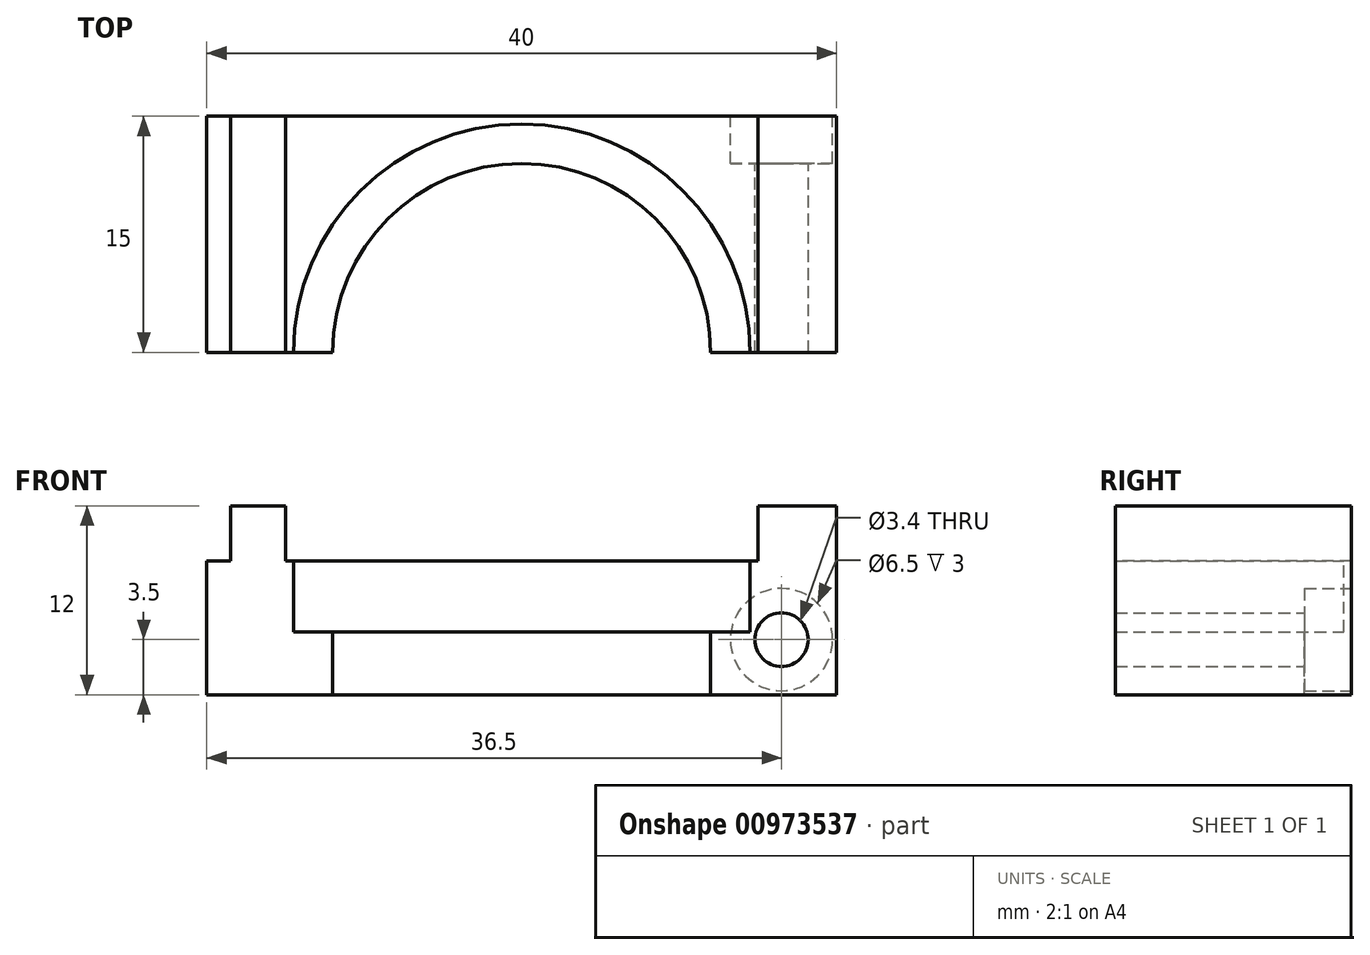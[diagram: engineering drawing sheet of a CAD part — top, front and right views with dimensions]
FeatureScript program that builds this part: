
annotation { "Feature Type Name" : "Feature", "Feature Type Description" : "" }
export const myFeature = defineFeature(function(context is Context, id is Id, definition is map)
    precondition{}
    {
        {
            var Q0;
            Q0=qCreatedBy(makeId("Top.planeOp"),FACE);
            var sketch = newSketch(context, id + "F0", { "sketchPlane" : qUnion([Q0])});
            skLineSegment(sketch, "E0.bottom", {"start": v(-20, 0) * mm, "end": v(20, 0) * mm});
            skLineSegment(sketch, "E0.top", {"start": v(-20, -15) * mm, "end": v(20, -15) * mm});
            skLineSegment(sketch, "E0.left", {"start": v(-20, 0) * mm, "end": v(-20, -15) * mm});
            skLineSegment(sketch, "E0.right", {"start": v(20, 0) * mm, "end": v(20, -15) * mm});
            skSolve(sketch);
        }
        {
            var Q0;
            Q0=makeQuery(id+"F0.imprint","IMPRINT",FACE,{"disambiguationData":[TD([[makeQuery(id+"F0.imprint","IMPRINT",EDGE,{"derivedFrom":sQuery(id+"F0.wireOp",EDGE,"E0.bottom")}),-1.0]])]});
            extrude(context, id + "F1", {"entities" : qUnion([Q0]), "depth" : 12 * mm, "offsetDistance" : 25 * mm});
        }
        {
            var Q0;
            Q0=makeQuery(id+"F1.opExtrude","CAP_FACE",FACE,{"disambiguationData":[OSD([sQuery(id+"F0.wireOp",EDGE,"E0.bottom"),sQuery(id+"F0.wireOp",EDGE,"E0.top"),sQuery(id+"F0.wireOp",EDGE,"E0.left"),sQuery(id+"F0.wireOp",EDGE,"E0.right")])],"isStart":false});
            var sketch = newSketch(context, id + "F2", { "sketchPlane" : qUnion([Q0])});
            skArc(sketch, "E1", {"start": v(14.5, -15) * mm, "mid": v(0, -0.5) * mm, "end": v(-14.5, -15) * mm});
            skSolve(sketch);
        }
        {
            var Q0;
            {var subQ0=sQuery(id+"F2.wireOp",EDGE,"E1");Q0=makeQuery(id+"F2.imprint","IMPRINT",FACE,{"disambiguationData":[TD([[makeQuery(id+"F2.imprint","IMPRINT",EDGE,{"derivedFrom":subQ0}),1.0]])]});}
            extrude(context, id + "F3", {"entities" : qUnion([Q0]), "operationType" : NewBodyOperationType.REMOVE, "oppositeDirection" : true, "depth" : 8 * mm, "offsetDistance" : 25 * mm});
        }
        {
            var Q0;
            Q0=makeQuery(id+"F3.boolean.opBoolean","COPY",FACE,{"derivedFrom":makeQuery(id+"F3.opExtrude","CAP_FACE",FACE,{"disambiguationData":[OSD([sQuery(id+"F0.wireOp",EDGE,"E0.top"),sQuery(id+"F2.wireOp",EDGE,"E1")])],"isStart":false})});
            var sketch = newSketch(context, id + "F4", { "sketchPlane" : qUnion([Q0])});
            skArc(sketch, "E2", {"start": v(12, -15) * mm, "mid": v(0, -3) * mm, "end": v(-12, -15) * mm});
            skSolve(sketch);
        }
        {
            var Q0;
            {var subQ0=sQuery(id+"F4.wireOp",EDGE,"E2");Q0=makeQuery(id+"F4.imprint","IMPRINT",FACE,{"disambiguationData":[TD([[makeQuery(id+"F4.imprint","IMPRINT",EDGE,{"derivedFrom":subQ0}),1.0]])]});}
            extrude(context, id + "F5", {"entities" : qUnion([Q0]), "operationType" : NewBodyOperationType.REMOVE, "endBound" : BoundingType.UP_TO_NEXT, "oppositeDirection" : true, "depth" : 25 * mm, "offsetDistance" : 25 * mm});
        }
        {
            var Q0;
            {var subQ1=sQuery(id+"F0.wireOp",EDGE,"E0.left");var subQ3=sQuery(id+"F0.wireOp",EDGE,"E0.top");Q0=makeQuery(id+"F5.boolean.opBoolean","SPLIT",FACE,{"disambiguationData":[TD([makeQuery(id+"F1.opExtrude","SWEPT_FACE",FACE,{"disambiguationData":[OSD([subQ1])]})])],"derivedFrom":makeQuery(id+"F1.opExtrude","SWEPT_FACE",FACE,{"disambiguationData":[OSD([subQ3])]})});}
            var sketch = newSketch(context, id + "F6", { "sketchPlane" : qUnion([Q0])});
            skLineSegment(sketch, "E3.bottom", {"start": v(-20, 12) * mm, "end": v(-18.5, 12) * mm});
            skLineSegment(sketch, "E3.top", {"start": v(-20, 8.5) * mm, "end": v(-18.5, 8.5) * mm});
            skLineSegment(sketch, "E3.left", {"start": v(-20, 12) * mm, "end": v(-20, 8.5) * mm});
            skLineSegment(sketch, "E3.right", {"start": v(-18.5, 12) * mm, "end": v(-18.5, 8.5) * mm});
            skSolve(sketch);
        }
        {
            var Q0;
            Q0=makeQuery(id+"F6.imprint","IMPRINT",FACE,{"disambiguationData":[TD([[makeQuery(id+"F6.imprint","IMPRINT",EDGE,{"derivedFrom":sQuery(id+"F6.wireOp",EDGE,"E3.bottom")}),-1.0]])]});
            extrude(context, id + "F7", {"entities" : qUnion([Q0]), "operationType" : NewBodyOperationType.REMOVE, "endBound" : BoundingType.UP_TO_NEXT, "oppositeDirection" : true, "depth" : 25 * mm, "offsetDistance" : 25 * mm});
        }
        {
            var Q0;
            {var subQ1=sQuery(id+"F0.wireOp",EDGE,"E0.left");var subQ3=sQuery(id+"F0.wireOp",EDGE,"E0.top");Q0=makeQuery(id+"F5.boolean.opBoolean","SPLIT",FACE,{"disambiguationData":[TD([makeQuery(id+"F1.opExtrude","SWEPT_FACE",FACE,{"disambiguationData":[OSD([subQ1])]})])],"derivedFrom":makeQuery(id+"F1.opExtrude","SWEPT_FACE",FACE,{"disambiguationData":[OSD([subQ3])]})});}
            var sketch = newSketch(context, id + "F8", { "sketchPlane" : qUnion([Q0])});
            skLineSegment(sketch, "E4.bottom", {"start": v(-15, 12) * mm, "end": v(15, 12) * mm});
            skLineSegment(sketch, "E4.top", {"start": v(-15, 8.5) * mm, "end": v(15, 8.5) * mm});
            skLineSegment(sketch, "E4.left", {"start": v(-15, 12) * mm, "end": v(-15, 8.5) * mm});
            skLineSegment(sketch, "E4.right", {"start": v(15, 12) * mm, "end": v(15, 8.5) * mm});
            skSolve(sketch);
        }
        {
            var Q0;
            Q0=makeQuery(id+"F8.imprint","IMPRINT",FACE,{"disambiguationData":[TD([[makeQuery(id+"F8.imprint","IMPRINT",EDGE,{"derivedFrom":sQuery(id+"F8.wireOp",EDGE,"E4.bottom")}),-1.0]])]});
            var Q1;
            Q1=makeQuery(id+"F1.opExtrude","SWEPT_FACE",FACE,{"disambiguationData":[OSD([sQuery(id+"F0.wireOp",EDGE,"E0.bottom")])]});
            extrude(context, id + "F9", {"entities" : qUnion([Q0]), "operationType" : NewBodyOperationType.REMOVE, "endBound" : BoundingType.UP_TO_SURFACE, "oppositeDirection" : true, "depth" : 25 * mm, "endBoundEntityFace" : qUnion([Q1]), "offsetDistance" : 25 * mm});
        }
        {
            var Q0;
            Q0=makeQuery(id+"F1.opExtrude","SWEPT_FACE",FACE,{"disambiguationData":[OSD([sQuery(id+"F0.wireOp",EDGE,"E0.bottom")])]});
            var sketch = newSketch(context, id + "F10", { "sketchPlane" : qUnion([Q0])});
            skPoint(sketch, "E5", {"position": v(-16.5, 3.5) * mm});
            skSolve(sketch);
        }
        {
            var Q0;
            Q0=sQuery(id+"F10.wireOp",VERTEX,"E5");
            var Q1;
            Q1=makeQuery(id+"F1.opExtrude","SWEPT_BODY",BODY,{"disambiguationData":[OSD([sQuery(id+"F0.wireOp",EDGE,"E0.bottom"),sQuery(id+"F0.wireOp",EDGE,"E0.top"),sQuery(id+"F0.wireOp",EDGE,"E0.left"),sQuery(id+"F0.wireOp",EDGE,"E0.right")])]});
            hole(context, id + "F11", {"style" : HoleStyle.C_BORE, "endStyle" : HoleEndStyle.THROUGH, "standardTappedOrClearance" : lookupTablePath({ "fit" : "Normal", "standard" : "ISO", "size" : "M3", "type" : "Clearance" }), "standardBlindInLast" : lookupTablePath({ "fit" : "Normal", "standard" : "ISO", "engagement" : "75%", "pitch" : "0.5 mm", "size" : "M3", "type" : "Clearance & tapped" }), "holeDiameter" : 3.4 * mm, "cBoreDiameter" : 6.5 * mm, "cBoreDepth" : 3 * mm, "majorDiameter" : 5 * mm, "isTappedThrough" : true, "tappedDepth" : 12 * mm, "tapClearance" : 3, "locations" : qUnion([Q0]), "scope" : qUnion([Q1])});
        }
    });
